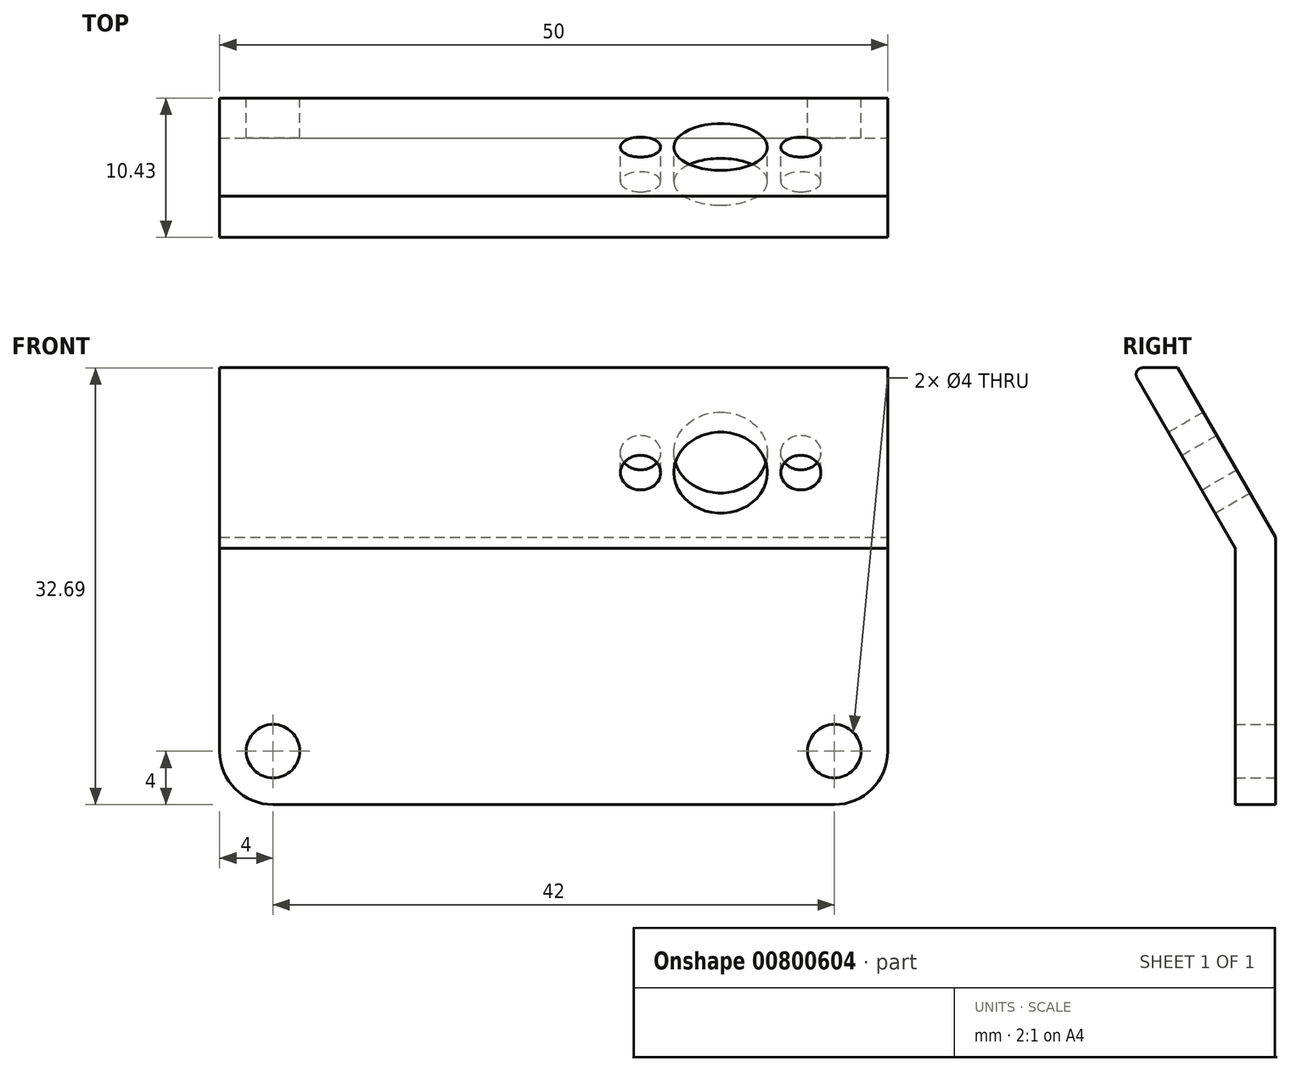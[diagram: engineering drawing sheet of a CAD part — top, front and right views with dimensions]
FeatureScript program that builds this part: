
annotation { "Feature Type Name" : "Feature", "Feature Type Description" : "" }
export const myFeature = defineFeature(function(context is Context, id is Id, definition is map)
    precondition{}
    {
        {
            var Q0;
            Q0=qCreatedBy(makeId("Front.planeOp"),FACE);
            var sketch = newSketch(context, id + "F0", { "sketchPlane" : qUnion([Q0])});
            skLineSegment(sketch, "E0.bottom", {"start": v(-25, 10) * mm, "end": v(25, 10) * mm});
            skLineSegment(sketch, "E0.top", {"start": v(-25, -10) * mm, "end": v(25, -10) * mm});
            skLineSegment(sketch, "E0.left", {"start": v(-25, 10) * mm, "end": v(-25, -10) * mm});
            skLineSegment(sketch, "E0.right", {"start": v(25, 10) * mm, "end": v(25, -10) * mm});
            skPoint(sketch, "E0.middle", {"position": v(0, 0) * mm});
            skCircle(sketch, "E1", {"center": v(-21, -6) * mm, "radius": 2 * mm});
            skCircle(sketch, "E2.MirrorC", {"center": v(21, -6) * mm, "radius": 2 * mm});
            skSolve(sketch);
        }
        {
            var Q0;
            Q0 = qSketchRegion(id + "F0", true);
            extrude(context, id + "F1", {"entities" : qUnion([Q0]), "depth" : 3 * mm, "offsetDistance" : 25 * mm});
        }
        {
            var Q0;
            Q0=makeQuery(id+"F1.opExtrude","SWEPT_EDGE",EDGE,{"disambiguationData":[OSD([sQuery(id+"F0.wireOp",EDGE,"E0.top"),sQuery(id+"F0.wireOp",EDGE,"E0.left")])]});
            var Q1;
            Q1=makeQuery(id+"F1.opExtrude","SWEPT_EDGE",EDGE,{"disambiguationData":[OSD([sQuery(id+"F0.wireOp",EDGE,"E0.top"),sQuery(id+"F0.wireOp",EDGE,"E0.right")])]});
            fillet(context, id + "F2", {"entities" : qUnion([Q0, Q1]), "radius" : 4 * mm, "tangentPropagation" : true, "allowEdgeOverflow" : false});
        }
        {
            var Q0;
            Q0=makeQuery(id+"F1.opExtrude","SWEPT_FACE",FACE,{"disambiguationData":[OSD([sQuery(id+"F0.wireOp",EDGE,"E0.right")])]});
            var sketch = newSketch(context, id + "F3", { "sketchPlane" : qUnion([Q0])});
            skLineSegment(sketch, "E3", {"start": v(-7.33, 22.7) * mm, "end": v(0, 10) * mm});
            skLineSegment(sketch, "E4", {"start": v(-3, 9.2) * mm, "end": v(-10.8, 22.7) * mm});
            skLineSegment(sketch, "E5", {"start": v(-10.8, 22.7) * mm, "end": v(-7.33, 22.7) * mm});
            skSolve(sketch);
        }
        {
            var Q0;
            Q0=makeQuery(id+"F3.imprint","IMPRINT",FACE,{"disambiguationData":[TD([[makeQuery(id+"F3.imprint","IMPRINT",EDGE,{"derivedFrom":sQuery(id+"F3.wireOp",EDGE,"E3")}),-1.0]])]});
            extrude(context, id + "F4", {"entities" : qUnion([Q0]), "operationType" : NewBodyOperationType.ADD, "depth" : -50 * mm, "offsetDistance" : 25 * mm});
        }
        {
            var Q0;
            Q0=makeQuery(id+"F4.opExtrude","SWEPT_FACE",FACE,{"disambiguationData":[OSD([sQuery(id+"F3.wireOp",EDGE,"E3")])]});
            var sketch = newSketch(context, id + "F5", { "sketchPlane" : qUnion([Q0])});
            skCircle(sketch, "E6", {"center": v(-12.5, 15.99) * mm, "radius": 3.5 * mm});
            skCircle(sketch, "E7", {"center": v(-6.5, 15.99) * mm, "radius": 1.5 * mm});
            skCircle(sketch, "E8", {"center": v(-18.5, 15.99) * mm, "radius": 1.5 * mm});
            skPoint(sketch, "E9", {"position": v(-25, 15.99) * mm});
            skPoint(sketch, "E10", {"position": v(25, 15.99) * mm});
            skLineSegment(sketch, "E11", {"start": v(25, 15.99) * mm, "end": v(-25, 15.99) * mm});
            skPoint(sketch, "E12", {"position": v(0, 15.99) * mm});
            skSolve(sketch);
        }
        {
            var Q0;
            Q0 = qSketchRegion(id + "F5", true);
            extrude(context, id + "F6", {"entities" : qUnion([Q0]), "operationType" : NewBodyOperationType.REMOVE, "oppositeDirection" : true, "depth" : 25 * mm, "offsetDistance" : 25 * mm});
        }
        {
            var Q0;
            Q0=makeQuery(id+"F4.opExtrude","SWEPT_EDGE",EDGE,{"disambiguationData":[OSD([sQuery(id+"F3.wireOp",EDGE,"E4"),sQuery(id+"F3.wireOp",EDGE,"E5")])]});
            fillet(context, id + "F7", {"entities" : qUnion([Q0]), "radius" : 0.5 * mm, "tangentPropagation" : true, "allowEdgeOverflow" : false});
        }
    });
